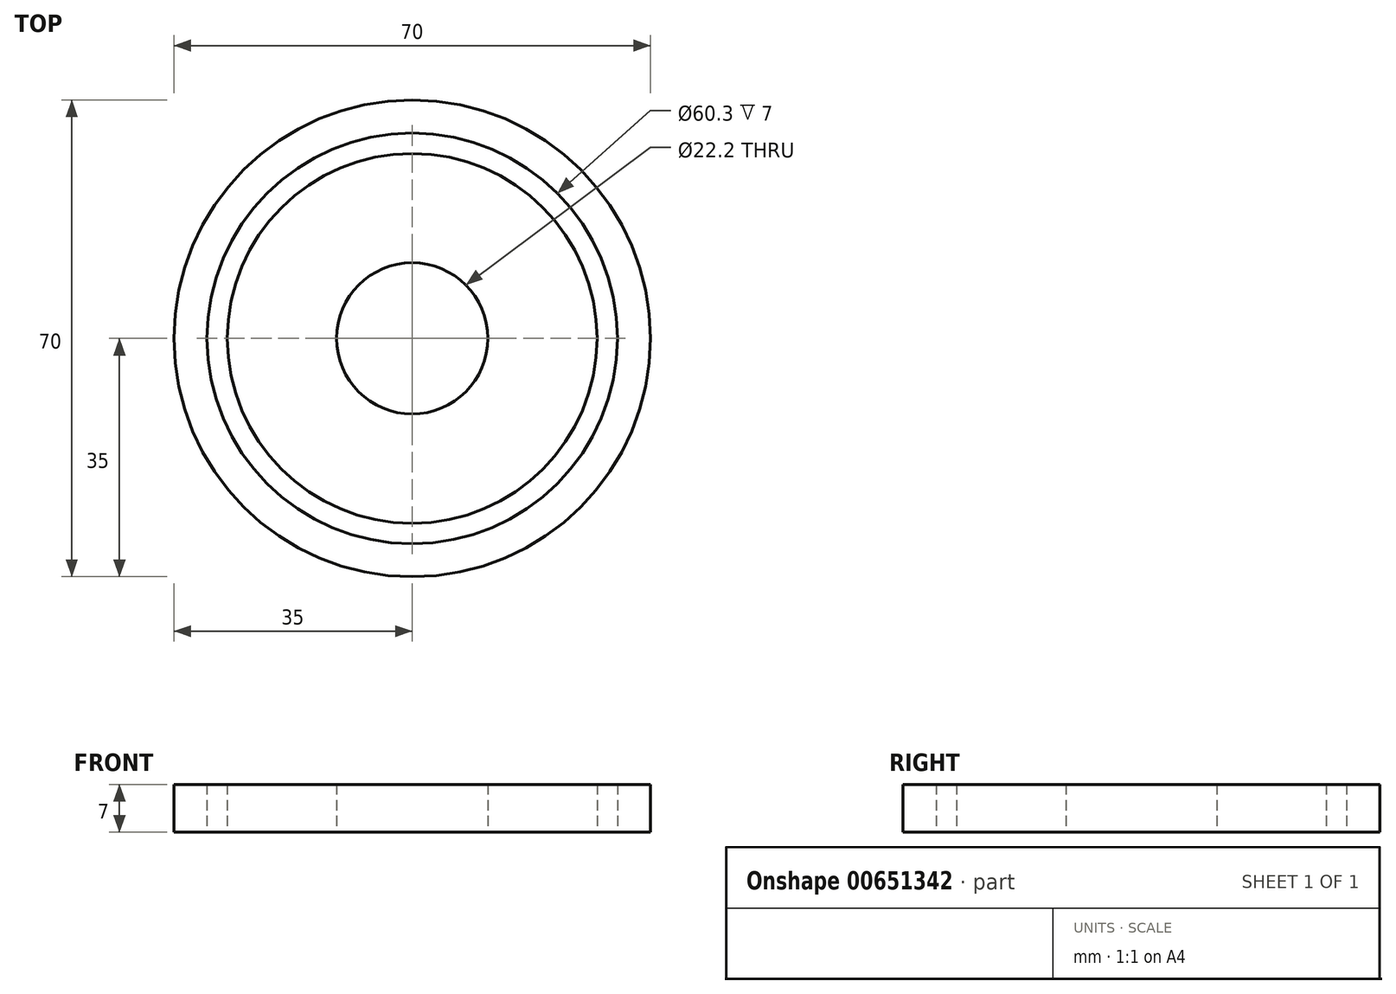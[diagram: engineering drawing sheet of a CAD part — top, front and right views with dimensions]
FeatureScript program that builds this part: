
annotation { "Feature Type Name" : "Feature", "Feature Type Description" : "" }
export const myFeature = defineFeature(function(context is Context, id is Id, definition is map)
    precondition{}
    {
        {
            var Q0;
            Q0=qCreatedBy(makeId("Top.planeOp"),FACE);
            var sketch = newSketch(context, id + "F0", { "sketchPlane" : qUnion([Q0])});
            skCircle(sketch, "E0", {"center": v(0, 0) * mm, "radius": 30.15 * mm});
            skCircle(sketch, "E1", {"center": v(0, 0) * mm, "radius": 27.15 * mm});
            skCircle(sketch, "E2", {"center": v(0, 0) * mm, "radius": 11.1 * mm});
            skCircle(sketch, "E3", {"center": v(0, 0) * mm, "radius": 35 * mm});
            skSolve(sketch);
        }
        {
            var Q0;
            Q0=makeQuery(id+"F0.imprint","IMPRINT",FACE,{"disambiguationData":[TD([[makeQuery(id+"F0.imprint","IMPRINT",EDGE,{"derivedFrom":sQuery(id+"F0.wireOp",EDGE,"E1")}),1.0]])]});
            var Q1;
            Q1=makeQuery(id+"F0.imprint","IMPRINT",FACE,{"disambiguationData":[TD([[makeQuery(id+"F0.imprint","IMPRINT",EDGE,{"derivedFrom":sQuery(id+"F0.wireOp",EDGE,"E0")}),-1.0]])]});
            extrude(context, id + "F1", {"entities" : qUnion([Q0, Q1]), "depth" : 7 * mm, "offsetDistance" : 25 * mm});
        }
    });
